# Revit family: 0051255 Lighting Fixture_Sylvania_Rana Linear MPO_Surface Mounted
name_source: partatom
category: Lighting Fixtures
revit_build: Autodesk Revit LT 2015 (Build: 20140606_1530(x64)
units: mm (PartAtom-declared; Revit-internal decimal feet)

## types (1)
- RANA LINEAR S 3KLM WW MPO 1-10 W
    Apparent Load = 29 VA
    Assembly Code = D5020200
    Body Material = Steel_Sylvania_Rana_White_RAL 9016
    CRI (Ra) = >80
    Catalog Number = 0051255 RANA LINEAR S 3KLM WW MPO 1-10 W
    Color Filter = 16777215
    Default Elevation = 0 mm  [stored 0 ft]
    Description = Slim Surface or Suspended luminaires Can be mounted individually or in continuous runs with seamless light effect; Long service life (50 000 hours) with great maintenance of the luminous flux (90 % of its initial value) Driver life-time : 50 000 hours / 10% max failure; 3 different optics offer 3 different light distributions with visual comfort and efficiency Colour Temperature Warm White (3000 K) or Neutral White (4000 K) Up to 3186lm (luminaire lumen output on RANA Linear Louvre + Prismatic Optic) High luminaire efficiency up to 127 lm/W (total system efficiency on RANA Linear Louvre + Prismatic Optic) Colour Rendering Index (Ra) > 80 for office applications LED Colour Consistency between multiple luminaires (chromaticity tolerance): 3 SDCM or 3-step MacAdam ellipse Sleek and unobtrusive square profile design, to mix and match recessed and / or surface luminaires in a single lighting scheme Colour: White RAL 9016 as standard, other colours on request Closed optical system with protective covers on LED modules Available in Constant Current, DALI (switchDIM), 1-10V or Organic Response dimming system and 3 hour emergency versions Low glare: UGR<19 with the Louvre + Primsatic Optic for Display Screen Equipment (DSE) workstations
    Diffuser Material = Polycarbonate_Sylvania_Rana_Clear
    Dimming Lamp Color Temperature Shift = <None>
    Distribution Type = Direct
    Drive Current = 217 mA
    Electrical Protection = CLASS I
    Emit Shape Visible in Rendering = No
    Emit from Rectangle Length = 75 mm
    Emit from Rectangle Width = 1130 mm  [stored 3.70735 ft]
    Energy Class = A++, A+, A
    Glare Control = UGR<21
    Glow Wire Test = 850 °C
    Height = 87 mm  [stored 0.285433 ft]
    IK Rating = IK07
    IP Rating = IP20
    LOR = 100%
    Lamp = Integrated LED
    Length = 1150 mm
    Life = 50 000h
    Manufacturer = Feilo Sylvania
    Model = RANA LINEAR S 3KLM WW MPO 1-10 W
    Photometric Web File = 0051255_RANALINEARS3KLMWWMPO1-10W-207205.ies
    Product Family = Rana Linear MPO
    Product Page URL = http://www.feilosylvania.com
    Reflector Material = Steel_Sylvania_Rana_Silver
    Ta Rating = -25°C to 30°C
    Tilt Angle = -90.00°
    URL = http://www.feilosylvania.com
    Voltage = 230 V
    Voltage Comments = UNV (Universal Voltage; 220-240 Volt)
    Weight = 3.00 kg
    Width = 87 mm  [stored 0.285433 ft]

note: [stored X ft] marks values corroborated as IEEE doubles in the binary element streams (Revit-internal decimal feet)

## geometry (parser evidence)
native form markers: Blend x24, Sweep x6
no freeform markers — native parametric forms only
